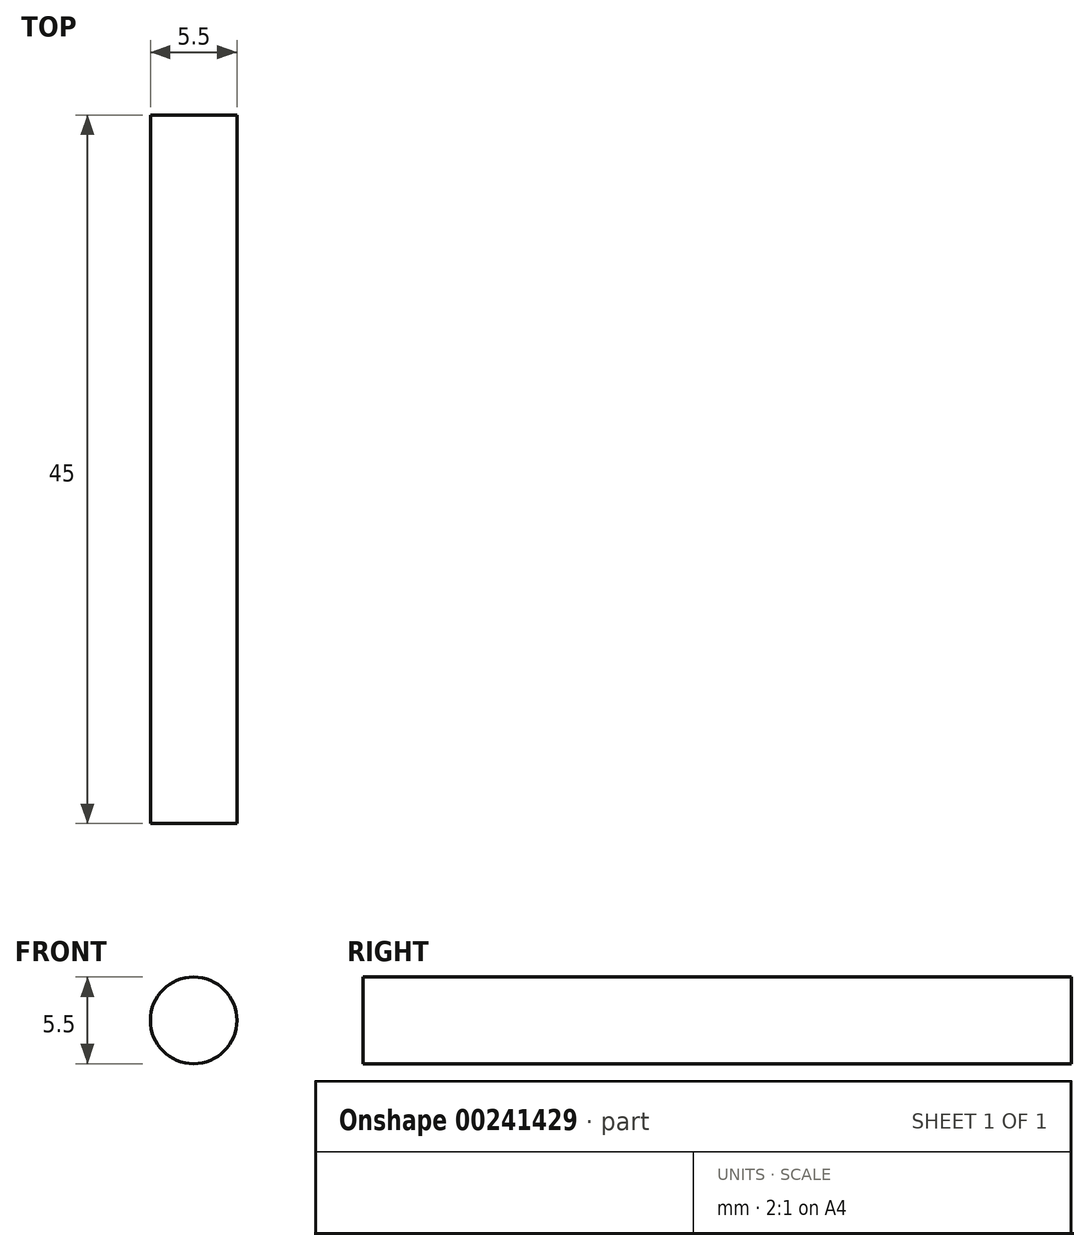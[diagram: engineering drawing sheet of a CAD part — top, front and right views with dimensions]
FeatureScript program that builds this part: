
annotation { "Feature Type Name" : "Feature", "Feature Type Description" : "" }
export const myFeature = defineFeature(function(context is Context, id is Id, definition is map)
    precondition{}
    {
        {
            var Q0;
            Q0=qCreatedBy(makeId("Front.planeOp"),FACE);
            var sketch = newSketch(context, id + "F0", { "sketchPlane" : qUnion([Q0])});
            skCircle(sketch, "E0", {"center": v(0, 0) * mm, "radius": 2.75 * mm});
            skSolve(sketch);
        }
        {
            var Q0;
            Q0 = qSketchRegion(id + "F0", true);
            extrude(context, id + "F1", {"entities" : qUnion([Q0]), "depth" : 45 * mm});
        }
    });
